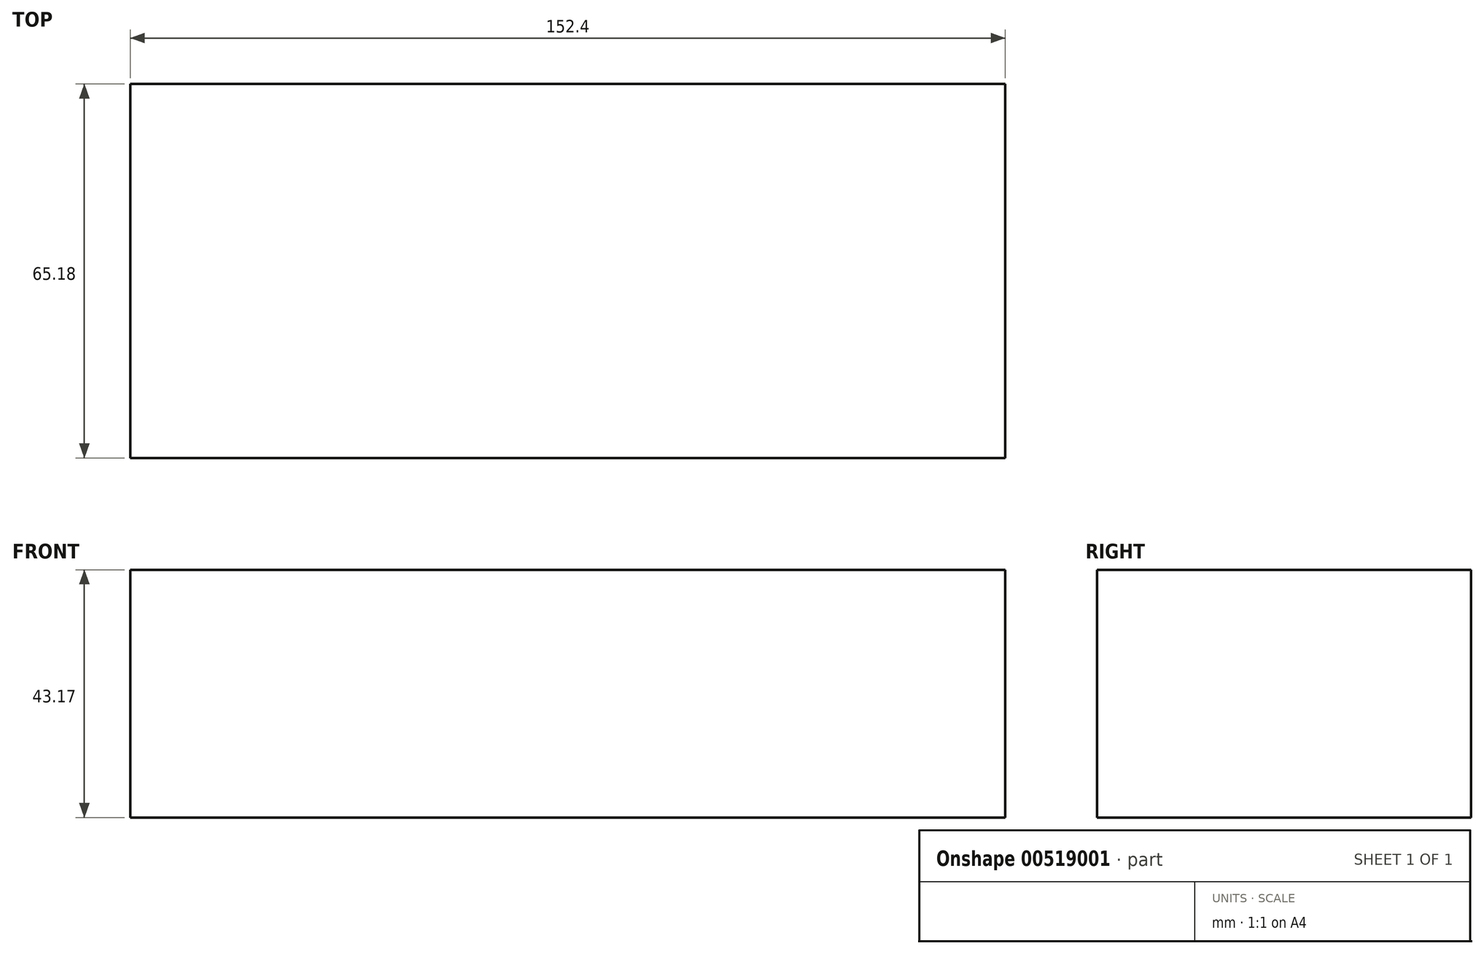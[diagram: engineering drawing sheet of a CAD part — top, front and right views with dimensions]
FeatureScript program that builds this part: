
annotation { "Feature Type Name" : "Feature", "Feature Type Description" : "" }
export const myFeature = defineFeature(function(context is Context, id is Id, definition is map)
    precondition{}
    {
        {
            var Q0;
            Q0=qCreatedBy(makeId("Right.planeOp"), FACE);
            var sketch = newSketch(context, id + "F0", { "sketchPlane" : qUnion([Q0])});
            skLineSegment(sketch, "E0.bottom", {"start": v(0, 0) * mm, "end": v(-65.18, 0) * mm});
            skLineSegment(sketch, "E0.top", {"start": v(0, -43.17) * mm, "end": v(-65.18, -43.17) * mm});
            skLineSegment(sketch, "E0.left", {"start": v(0, 0) * mm, "end": v(0, -43.17) * mm});
            skLineSegment(sketch, "E0.right", {"start": v(-65.18, 0) * mm, "end": v(-65.18, -43.17) * mm});
            skSolve(sketch);
        }
        {
            var Q0;
            Q0 = qSketchRegion(id + "F0", true);
            extrude(context, id + "F1", {"entities" : qUnion([Q0]), "depth" : 152.4 * mm, "offsetDistance" : 25.4 * mm});
        }
    });
